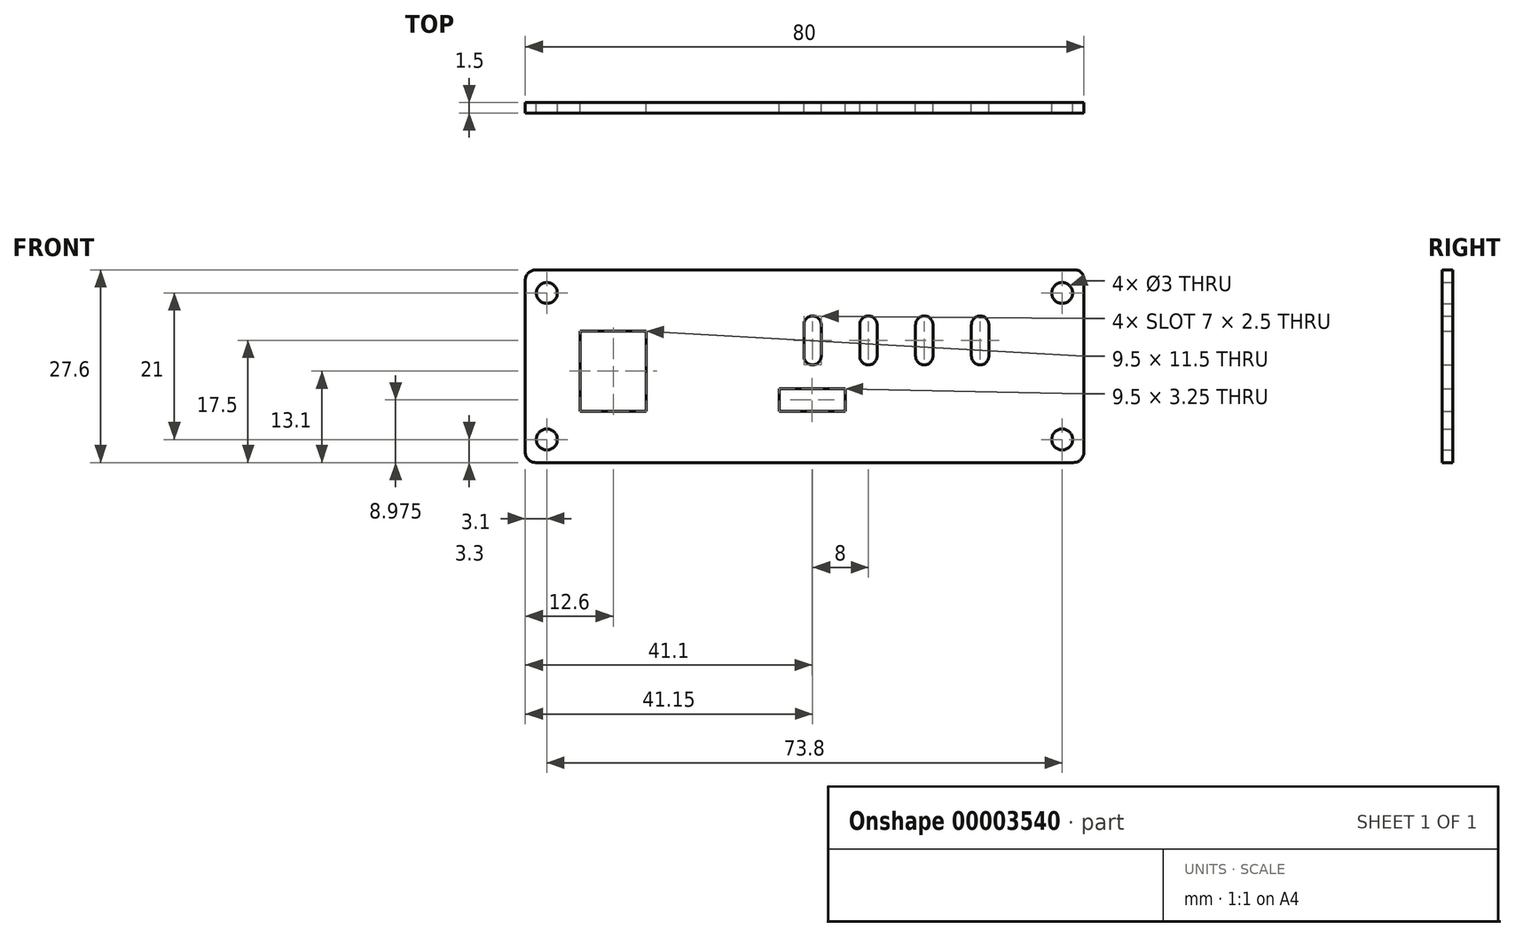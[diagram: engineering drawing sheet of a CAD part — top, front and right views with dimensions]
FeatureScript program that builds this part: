
annotation { "Feature Type Name" : "Feature", "Feature Type Description" : "" }
export const myFeature = defineFeature(function(context is Context, id is Id, definition is map)
    precondition{}
    {
        {
            var Q0;
            Q0=qCreatedBy(makeId("Front.planeOp"),FACE);
            var sketch = newSketch(context, id + "F0", { "sketchPlane" : qUnion([Q0])});
            skLineSegment(sketch, "E0.bottom", {"start": v(1.5, 0) * mm, "end": v(78.5, 0) * mm});
            skLineSegment(sketch, "E0.top", {"start": v(1.5, 27.6) * mm, "end": v(78.75, 27.6) * mm});
            skLineSegment(sketch, "E0.left", {"start": v(0, 1.5) * mm, "end": v(0, 26.1) * mm});
            skLineSegment(sketch, "E0.right", {"start": v(80, 1.5) * mm, "end": v(80, 26.35) * mm});
            skCircle(sketch, "E1", {"center": v(3.1, 3.3) * mm, "radius": 1.5 * mm});
            skCircle(sketch, "E2", {"center": v(76.9, 3.3) * mm, "radius": 1.5 * mm});
            skCircle(sketch, "E3", {"center": v(76.9, 24.3) * mm, "radius": 1.5 * mm});
            skCircle(sketch, "E4", {"center": v(3.1, 24.3) * mm, "radius": 1.5 * mm});
            skLineSegment(sketch, "E5.bottom", {"start": v(7.85, 18.85) * mm, "end": v(17.35, 18.85) * mm});
            skLineSegment(sketch, "E5.top", {"start": v(7.85, 7.35) * mm, "end": v(17.35, 7.35) * mm});
            skLineSegment(sketch, "E5.left", {"start": v(7.85, 18.85) * mm, "end": v(7.85, 7.35) * mm});
            skLineSegment(sketch, "E5.right", {"start": v(17.35, 18.85) * mm, "end": v(17.35, 7.35) * mm});
            skLineSegment(sketch, "E6.bottom", {"start": v(36.35, 10.6) * mm, "end": v(45.85, 10.6) * mm});
            skLineSegment(sketch, "E6.top", {"start": v(36.35, 7.35) * mm, "end": v(45.85, 7.35) * mm});
            skLineSegment(sketch, "E6.left", {"start": v(36.35, 10.6) * mm, "end": v(36.35, 7.35) * mm});
            skLineSegment(sketch, "E6.right", {"start": v(45.85, 10.6) * mm, "end": v(45.85, 7.35) * mm});
            skLineSegment(sketch, "E7.bottom", {"start": v(65.15, 21) * mm, "end": v(65.15, 21) * mm});
            skLineSegment(sketch, "E7.top", {"start": v(65.15, 14) * mm, "end": v(65.15, 14) * mm});
            skLineSegment(sketch, "E7.left", {"start": v(66.4, 19.75) * mm, "end": v(66.4, 15.25) * mm});
            skLineSegment(sketch, "E7.right", {"start": v(63.9, 19.75) * mm, "end": v(63.9, 15.25) * mm});
            skLineSegment(sketch, "E8.1.0.0", {"start": v(57.15, 14) * mm, "end": v(57.15, 14) * mm});
            skLineSegment(sketch, "E8.1.0.1", {"start": v(55.9, 19.75) * mm, "end": v(55.9, 15.25) * mm});
            skLineSegment(sketch, "E8.1.0.2", {"start": v(57.15, 21) * mm, "end": v(57.15, 21) * mm});
            skLineSegment(sketch, "E8.1.0.3", {"start": v(58.4, 19.75) * mm, "end": v(58.4, 15.25) * mm});
            skLineSegment(sketch, "E8.2.0.0", {"start": v(49.15, 14) * mm, "end": v(49.15, 14) * mm});
            skLineSegment(sketch, "E8.2.0.1", {"start": v(47.9, 19.75) * mm, "end": v(47.9, 15.25) * mm});
            skLineSegment(sketch, "E8.2.0.2", {"start": v(49.15, 21) * mm, "end": v(49.15, 21) * mm});
            skLineSegment(sketch, "E8.2.0.3", {"start": v(50.4, 19.75) * mm, "end": v(50.4, 15.25) * mm});
            skLineSegment(sketch, "E8.3.0.0", {"start": v(41.15, 14) * mm, "end": v(41.15, 14) * mm});
            skLineSegment(sketch, "E8.3.0.1", {"start": v(39.9, 19.75) * mm, "end": v(39.9, 15.25) * mm});
            skLineSegment(sketch, "E8.3.0.2", {"start": v(41.15, 21) * mm, "end": v(41.15, 21) * mm});
            skLineSegment(sketch, "E8.3.0.3", {"start": v(42.4, 19.75) * mm, "end": v(42.4, 15.25) * mm});
            skLineSegment(sketch, "E8.direction1", {"start": v(63.9, 14) * mm, "end": v(55.9, 14) * mm, "construction": true});
            skPoint(sketch, "E9.visualSharp", {"position": v(80, 27.6) * mm});
            skArc(sketch, "E9.filletArc", {"start": v(80, 26.35) * mm, "mid": v(79.63, 27.23) * mm, "end": v(78.75, 27.6) * mm});
            skPoint(sketch, "E10.visualSharp", {"position": v(66.4, 21) * mm});
            skArc(sketch, "E10.filletArc", {"start": v(66.4, 19.75) * mm, "mid": v(66.03, 20.63) * mm, "end": v(65.15, 21) * mm});
            skPoint(sketch, "E11.visualSharp", {"position": v(63.9, 21) * mm});
            skArc(sketch, "E11.filletArc", {"start": v(65.15, 21) * mm, "mid": v(64.27, 20.63) * mm, "end": v(63.9, 19.75) * mm});
            skPoint(sketch, "E12.visualSharp", {"position": v(63.9, 14) * mm});
            skArc(sketch, "E12.filletArc", {"start": v(63.9, 15.25) * mm, "mid": v(64.27, 14.37) * mm, "end": v(65.15, 14) * mm});
            skPoint(sketch, "E13.visualSharp", {"position": v(66.4, 14) * mm});
            skArc(sketch, "E13.filletArc", {"start": v(65.15, 14) * mm, "mid": v(66.03, 14.37) * mm, "end": v(66.4, 15.25) * mm});
            skPoint(sketch, "E14.visualSharp", {"position": v(58.4, 21) * mm});
            skArc(sketch, "E14.filletArc", {"start": v(58.4, 19.75) * mm, "mid": v(58.03, 20.63) * mm, "end": v(57.15, 21) * mm});
            skPoint(sketch, "E15.visualSharp", {"position": v(55.9, 21) * mm});
            skArc(sketch, "E15.filletArc", {"start": v(57.15, 21) * mm, "mid": v(56.27, 20.63) * mm, "end": v(55.9, 19.75) * mm});
            skPoint(sketch, "E16.visualSharp", {"position": v(55.9, 14) * mm});
            skArc(sketch, "E16.filletArc", {"start": v(55.9, 15.25) * mm, "mid": v(56.27, 14.37) * mm, "end": v(57.15, 14) * mm});
            skPoint(sketch, "E17.visualSharp", {"position": v(58.4, 14) * mm});
            skArc(sketch, "E17.filletArc", {"start": v(57.15, 14) * mm, "mid": v(58.03, 14.37) * mm, "end": v(58.4, 15.25) * mm});
            skPoint(sketch, "E18.visualSharp", {"position": v(47.9, 21) * mm});
            skArc(sketch, "E18.filletArc", {"start": v(49.15, 21) * mm, "mid": v(48.27, 20.63) * mm, "end": v(47.9, 19.75) * mm});
            skPoint(sketch, "E19.visualSharp", {"position": v(50.4, 21) * mm});
            skArc(sketch, "E19.filletArc", {"start": v(50.4, 19.75) * mm, "mid": v(50.03, 20.63) * mm, "end": v(49.15, 21) * mm});
            skPoint(sketch, "E20.visualSharp", {"position": v(50.4, 14) * mm});
            skArc(sketch, "E20.filletArc", {"start": v(49.15, 14) * mm, "mid": v(50.03, 14.37) * mm, "end": v(50.4, 15.25) * mm});
            skPoint(sketch, "E21.visualSharp", {"position": v(47.9, 14) * mm});
            skArc(sketch, "E21.filletArc", {"start": v(47.9, 15.25) * mm, "mid": v(48.27, 14.37) * mm, "end": v(49.15, 14) * mm});
            skPoint(sketch, "E22.visualSharp", {"position": v(42.4, 21) * mm});
            skArc(sketch, "E22.filletArc", {"start": v(42.4, 19.75) * mm, "mid": v(42.03, 20.63) * mm, "end": v(41.15, 21) * mm});
            skPoint(sketch, "E23.visualSharp", {"position": v(39.9, 21) * mm});
            skArc(sketch, "E23.filletArc", {"start": v(41.15, 21) * mm, "mid": v(40.27, 20.63) * mm, "end": v(39.9, 19.75) * mm});
            skPoint(sketch, "E24.visualSharp", {"position": v(39.9, 14) * mm});
            skArc(sketch, "E24.filletArc", {"start": v(39.9, 15.25) * mm, "mid": v(40.27, 14.37) * mm, "end": v(41.15, 14) * mm});
            skPoint(sketch, "E25.visualSharp", {"position": v(42.4, 14) * mm});
            skArc(sketch, "E25.filletArc", {"start": v(41.15, 14) * mm, "mid": v(42.03, 14.37) * mm, "end": v(42.4, 15.25) * mm});
            skPoint(sketch, "E26.visualSharp", {"position": v(80, 0) * mm});
            skArc(sketch, "E26.filletArc", {"start": v(78.5, 0) * mm, "mid": v(79.56, 0.44) * mm, "end": v(80, 1.5) * mm});
            skPoint(sketch, "E27.visualSharp", {"position": v(0, 27.6) * mm});
            skArc(sketch, "E27.filletArc", {"start": v(1.5, 27.6) * mm, "mid": v(0.44, 27.16) * mm, "end": v(0, 26.1) * mm});
            skPoint(sketch, "E28.visualSharp", {"position": v(0, 0) * mm});
            skArc(sketch, "E28.filletArc", {"start": v(0, 1.5) * mm, "mid": v(0.44, 0.44) * mm, "end": v(1.5, 0) * mm});
            skSolve(sketch);
        }
        {
            var Q0;
            Q0 = qSketchRegion(id + "F0", true);
            extrude(context, id + "F1", {"entities" : qUnion([Q0]), "depth" : 1.5 * mm});
        }
    });
